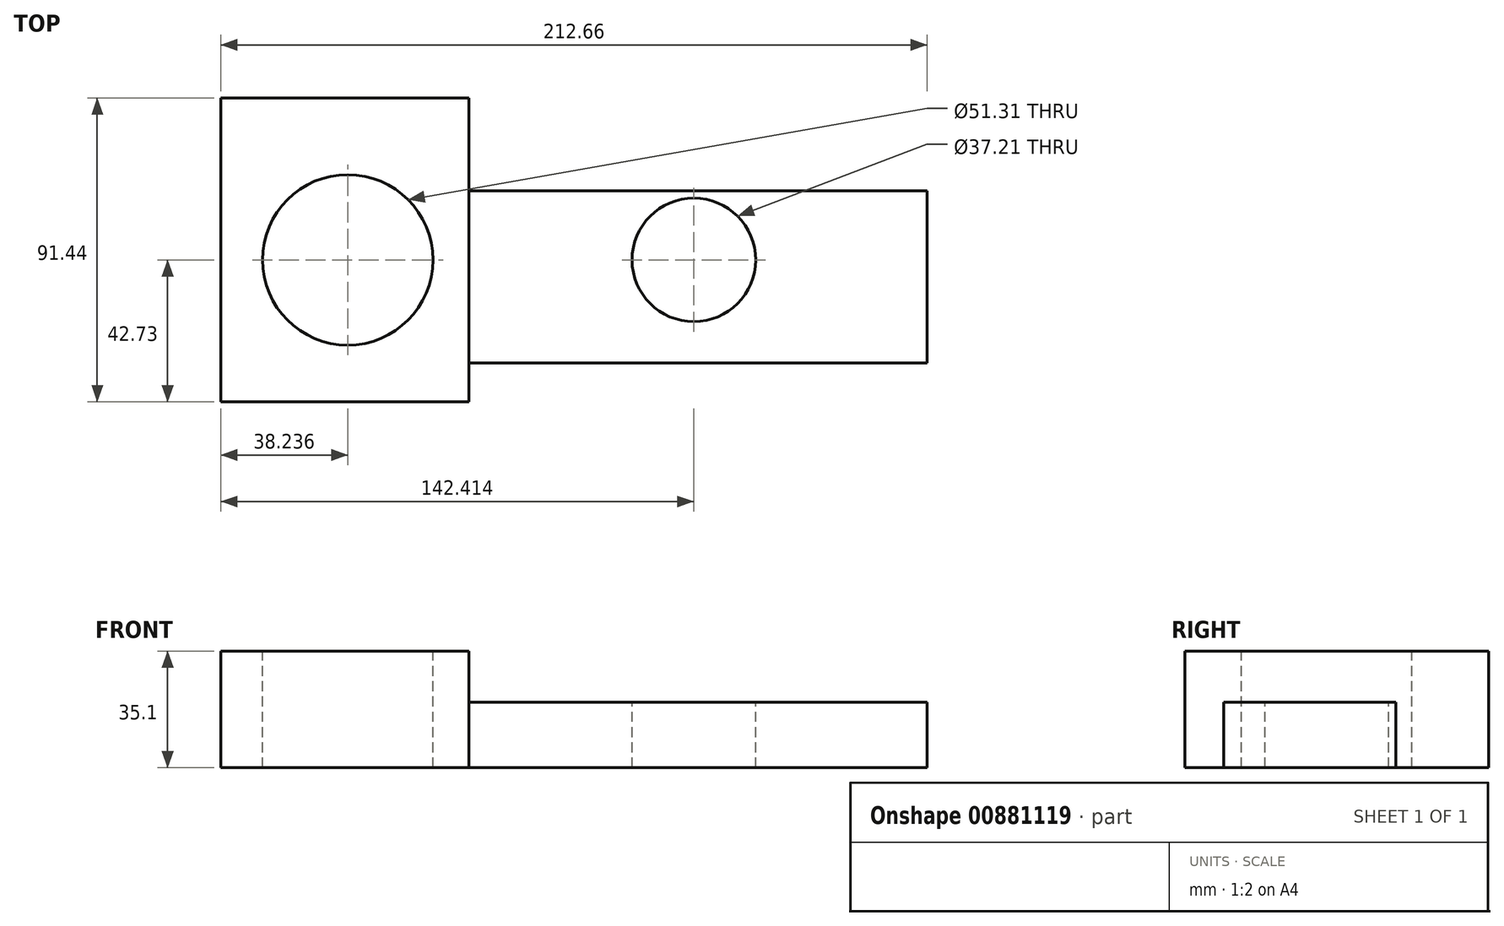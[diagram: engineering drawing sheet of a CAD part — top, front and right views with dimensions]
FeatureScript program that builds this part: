
annotation { "Feature Type Name" : "Feature", "Feature Type Description" : "" }
export const myFeature = defineFeature(function(context is Context, id is Id, definition is map)
    precondition{}
    {
        {
            var Q0;
            Q0=qCreatedBy(makeId("Right.planeOp"),FACE);
            var sketch = newSketch(context, id + "F0", { "sketchPlane" : qUnion([Q0])});
            skLineSegment(sketch, "E0.bottom", {"start": v(-42.73, 22.1) * mm, "end": v(48.71, 22.1) * mm});
            skLineSegment(sketch, "E0.top", {"start": v(-42.73, 57.19) * mm, "end": v(48.71, 57.19) * mm});
            skLineSegment(sketch, "E0.left", {"start": v(-42.73, 22.1) * mm, "end": v(-42.73, 57.19) * mm});
            skLineSegment(sketch, "E0.right", {"start": v(48.71, 22.1) * mm, "end": v(48.71, 57.19) * mm});
            skSolve(sketch);
        }
        {
            var Q0;
            Q0=makeQuery(id+"F0.imprint","IMPRINT",FACE,{"disambiguationData":[TD([[makeQuery(id+"F0.imprint","IMPRINT",EDGE,{"derivedFrom":sQuery(id+"F0.wireOp",EDGE,"E0.bottom")}),1.0]])]});
            extrude(context, id + "F1", {"entities" : qUnion([Q0]), "depth" : 74.66 * mm, "offsetDistance" : 25.4 * mm});
        }
        {
            var Q0;
            Q0=makeQuery(id+"F1.opExtrude","SWEPT_FACE",FACE,{"disambiguationData":[OSD([sQuery(id+"F0.wireOp",EDGE,"E0.top")])]});
            var sketch = newSketch(context, id + "F2", { "sketchPlane" : qUnion([Q0])});
            skCircle(sketch, "E1", {"center": v(38.24, 0) * mm, "radius": 25.66 * mm});
            skSolve(sketch);
        }
        {
            var Q0;
            Q0 = qSketchRegion(id + "F2", true);
            extrude(context, id + "F3", {"entities" : qUnion([Q0]), "operationType" : NewBodyOperationType.REMOVE, "oppositeDirection" : true, "depth" : 59.96 * mm, "offsetDistance" : 25.4 * mm});
        }
        {
            var Q0;
            Q0=makeQuery(id+"F1.opExtrude","CAP_FACE",FACE,{"disambiguationData":[OSD([sQuery(id+"F0.wireOp",EDGE,"E0.bottom"),sQuery(id+"F0.wireOp",EDGE,"E0.top"),sQuery(id+"F0.wireOp",EDGE,"E0.left"),sQuery(id+"F0.wireOp",EDGE,"E0.right")])],"isStart":false});
            var sketch = newSketch(context, id + "F4", { "sketchPlane" : qUnion([Q0])});
            skLineSegment(sketch, "E2.bottom", {"start": v(20.79, 41.77) * mm, "end": v(-31.03, 41.77) * mm});
            skLineSegment(sketch, "E2.top", {"start": v(20.79, 22.1) * mm, "end": v(-31.03, 22.1) * mm});
            skLineSegment(sketch, "E2.left", {"start": v(20.79, 41.77) * mm, "end": v(20.79, 22.1) * mm});
            skLineSegment(sketch, "E2.right", {"start": v(-31.03, 41.77) * mm, "end": v(-31.03, 22.1) * mm});
            skSolve(sketch);
        }
        {
            var Q0;
            Q0 = qSketchRegion(id + "F4", true);
            extrude(context, id + "F5", {"entities" : qUnion([Q0]), "operationType" : NewBodyOperationType.ADD, "depth" : 138 * mm, "offsetDistance" : 25.4 * mm});
        }
        {
            var Q0;
            Q0=makeQuery(id+"F5.opExtrude","SWEPT_FACE",FACE,{"disambiguationData":[OSD([sQuery(id+"F4.wireOp",EDGE,"E2.bottom")])]});
            var sketch = newSketch(context, id + "F6", { "sketchPlane" : qUnion([Q0])});
            skCircle(sketch, "E3", {"center": v(142.41, 0) * mm, "radius": 18.6 * mm});
            skSolve(sketch);
        }
        {
            var Q0;
            Q0 = qSketchRegion(id + "F6", true);
            extrude(context, id + "F7", {"entities" : qUnion([Q0]), "operationType" : NewBodyOperationType.REMOVE, "oppositeDirection" : true, "depth" : 87.08 * mm, "offsetDistance" : 25.4 * mm});
        }
    });
